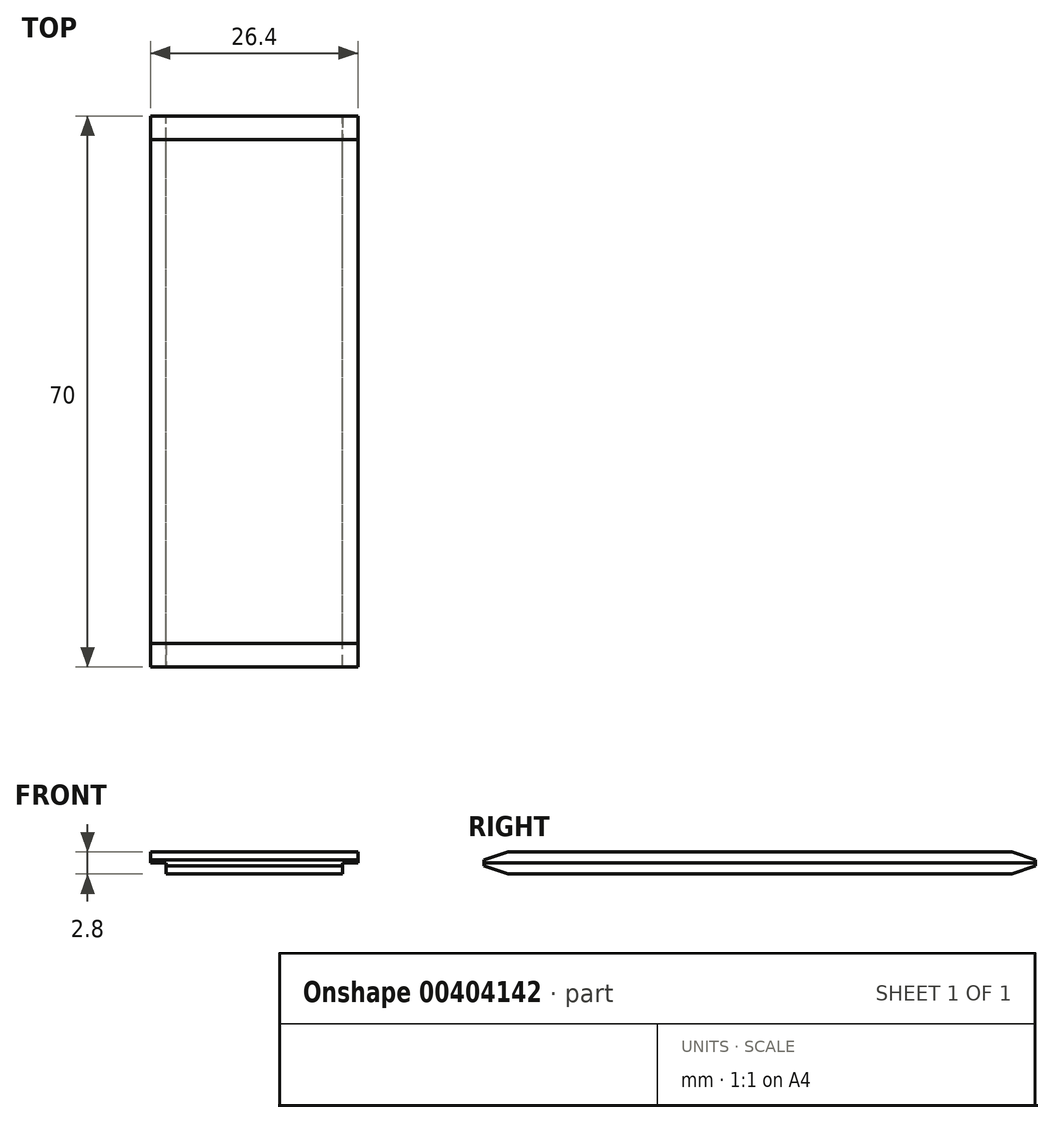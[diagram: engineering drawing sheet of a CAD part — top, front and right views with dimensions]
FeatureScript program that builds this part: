
annotation { "Feature Type Name" : "Feature", "Feature Type Description" : "" }
export const myFeature = defineFeature(function(context is Context, id is Id, definition is map)
    precondition{}
    {
        {
            var Q0;
            Q0=qCreatedBy(makeId("Front.planeOp"),FACE);
            var sketch = newSketch(context, id + "F0", { "sketchPlane" : qUnion([Q0])});
            skLineSegment(sketch, "E0", {"start": v(-16.4, -8.8) * mm, "end": v(16.4, -8.8) * mm});
            skLineSegment(sketch, "E1", {"start": v(16.4, -8.8) * mm, "end": v(19.4, 0) * mm});
            skLineSegment(sketch, "E2", {"start": v(19.4, 0) * mm, "end": v(20.8, 0) * mm});
            skLineSegment(sketch, "E3", {"start": v(20.8, 0) * mm, "end": v(17.55, -10.2) * mm});
            skLineSegment(sketch, "E4", {"start": v(17.55, -10.2) * mm, "end": v(-17.25, -10.2) * mm});
            skLineSegment(sketch, "E5", {"start": v(-17.25, -10.2) * mm, "end": v(-20.8, 0) * mm});
            skLineSegment(sketch, "E6", {"start": v(-20.8, 0) * mm, "end": v(-19.4, 0) * mm});
            skLineSegment(sketch, "E7", {"start": v(-16.4, -8.8) * mm, "end": v(-19.4, 0) * mm});
            skLineSegment(sketch, "E8", {"start": v(13.2, -10.2) * mm, "end": v(13.2, -11.6) * mm});
            skLineSegment(sketch, "E9", {"start": v(13.2, -11.6) * mm, "end": v(11.2, -11.6) * mm});
            skLineSegment(sketch, "E10", {"start": v(11.2, -11.6) * mm, "end": v(11.2, -13) * mm});
            skLineSegment(sketch, "E11", {"start": v(11.2, -13) * mm, "end": v(16.4, -13) * mm});
            skLineSegment(sketch, "E12", {"start": v(16.4, -13) * mm, "end": v(16.4, -10.2) * mm});
            skLineSegment(sketch, "E13", {"start": v(-16.4, -10.2) * mm, "end": v(-16.4, -13) * mm});
            skLineSegment(sketch, "E14", {"start": v(-16.4, -13) * mm, "end": v(-11.2, -13) * mm});
            skLineSegment(sketch, "E15", {"start": v(-11.2, -13) * mm, "end": v(-11.2, -11.6) * mm});
            skLineSegment(sketch, "E16", {"start": v(-11.2, -11.6) * mm, "end": v(-13.2, -11.6) * mm});
            skLineSegment(sketch, "E17", {"start": v(-13.2, -11.6) * mm, "end": v(-13.2, -10.2) * mm});
            skLineSegment(sketch, "E18", {"start": v(0, 0) * mm, "end": v(0, -36.82) * mm});
            skLineSegment(sketch, "E19", {"start": v(-11.2, -13) * mm, "end": v(11.2, -13) * mm});
            skLineSegment(sketch, "E20", {"start": v(-186.34, 341.2) * mm, "end": v(213.87, 341.2) * mm});
            skSolve(sketch);
        }
        {
            var Q0;
            {var subQ4=sQuery(id+"F0.wireOp",EDGE,"E8");Q0=makeQuery(id+"F0.imprint","IMPRINT",FACE,{"disambiguationData":[TD([[makeQuery(id+"F0.imprint","IMPRINT",EDGE,{"derivedFrom":subQ4}),-1.0]])]});}
            var Q1;
            {var subQ0=sQuery(id+"F0.wireOp",EDGE,"E15");Q1=makeQuery(id+"F0.imprint","IMPRINT",FACE,{"disambiguationData":[TD([[makeQuery(id+"F0.imprint","IMPRINT",EDGE,{"derivedFrom":subQ0}),-1.0]])]});}
            extrude(context, id + "F1", {"entities" : qUnion([Q0, Q1]), "depth" : 70 * mm});
        }
        {
            var Q0;
            Q0=makeQuery(id+"F1.opExtrude","CAP_EDGE",EDGE,{"disambiguationData":[OSD([sQuery(id+"F0.wireOp",EDGE,"E19")])],"isStart":false});
            var Q1;
            Q1=makeQuery(id+"F1.opExtrude","CAP_EDGE",EDGE,{"disambiguationData":[OSD([sQuery(id+"F0.wireOp",EDGE,"E4")])],"isStart":false});
            chamfer(context, id + "F2", {"entities" : qUnion([Q0, Q1]), "chamferType" : ChamferType.TWO_OFFSETS, "width1" : 1 * mm, "oppositeDirection" : false, "width2" : 3 * mm, "tangentPropagation" : true});
        }
        {
            var Q0;
            Q0=makeQuery(id+"F1.opExtrude","CAP_EDGE",EDGE,{"disambiguationData":[OSD([sQuery(id+"F0.wireOp",EDGE,"E4")])],"isStart":true});
            var Q1;
            Q1=makeQuery(id+"F1.opExtrude","CAP_EDGE",EDGE,{"disambiguationData":[OSD([sQuery(id+"F0.wireOp",EDGE,"E19")])],"isStart":true});
            chamfer(context, id + "F3", {"entities" : qUnion([Q0, Q1]), "chamferType" : ChamferType.TWO_OFFSETS, "width1" : 3 * mm, "oppositeDirection" : false, "width2" : 1 * mm, "tangentPropagation" : true});
        }
    });
